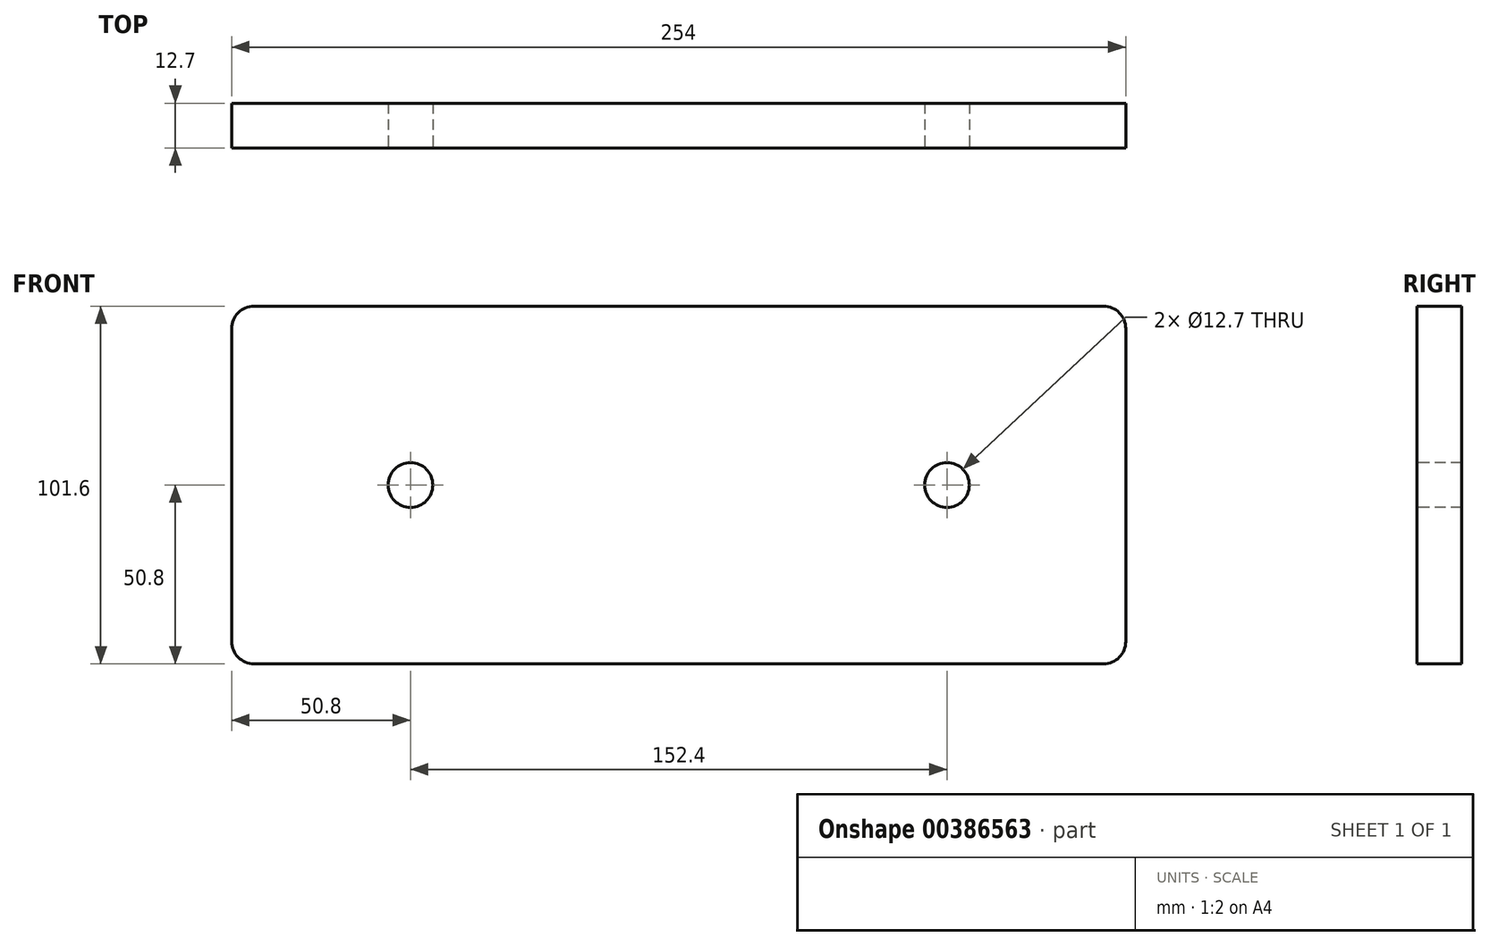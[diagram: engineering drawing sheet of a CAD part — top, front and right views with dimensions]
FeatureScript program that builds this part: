
annotation { "Feature Type Name" : "Feature", "Feature Type Description" : "" }
export const myFeature = defineFeature(function(context is Context, id is Id, definition is map)
    precondition{}
    {
        {
            var Q0;
            Q0=qCreatedBy(makeId("Front.planeOp"),FACE);
            var sketch = newSketch(context, id + "F0", { "sketchPlane" : qUnion([Q0])});
            skLineSegment(sketch, "E0.bottom", {"start": v(0, 0) * mm, "end": v(254, 0) * mm});
            skLineSegment(sketch, "E0.top", {"start": v(0, 101.6) * mm, "end": v(254, 101.6) * mm});
            skLineSegment(sketch, "E0.left", {"start": v(0, 0) * mm, "end": v(0, 101.6) * mm});
            skLineSegment(sketch, "E0.right", {"start": v(254, 0) * mm, "end": v(254, 101.6) * mm});
            skSolve(sketch);
        }
        {
            var Q0;
            Q0 = qSketchRegion(id + "F0", true);
            extrude(context, id + "F1", {"entities" : qUnion([Q0]), "depth" : 12.7 * mm});
        }
        {
            var Q0;
            Q0=makeQuery(id+"F1.opExtrude","CAP_FACE",FACE,{"disambiguationData":[OSD([sQuery(id+"F0.wireOp",EDGE,"E0.bottom"),sQuery(id+"F0.wireOp",EDGE,"E0.top"),sQuery(id+"F0.wireOp",EDGE,"E0.left"),sQuery(id+"F0.wireOp",EDGE,"E0.right")])],"isStart":false});
            var sketch = newSketch(context, id + "F2", { "sketchPlane" : qUnion([Q0])});
            skPoint(sketch, "E1", {"position": v(50.8, 50.8) * mm});
            skPoint(sketch, "E2", {"position": v(203.2, 50.8) * mm});
            skSolve(sketch);
        }
        {
            var Q0;
            Q0=sQuery(id+"F2.wireOp",VERTEX,"E1");
            var Q1;
            Q1=sQuery(id+"F2.wireOp",VERTEX,"E2");
            var Q2;
            Q2=makeQuery(id+"F1.opExtrude","SWEPT_BODY",BODY,{"disambiguationData":[OSD([sQuery(id+"F0.wireOp",EDGE,"E0.bottom"),sQuery(id+"F0.wireOp",EDGE,"E0.top"),sQuery(id+"F0.wireOp",EDGE,"E0.left"),sQuery(id+"F0.wireOp",EDGE,"E0.right")])]});
            hole(context, id + "F3", {"style" : HoleStyle.SIMPLE, "endStyle" : HoleEndStyle.THROUGH, "holeDiameter" : 12.7 * mm, "isTappedThrough" : true, "tappedDepth" : 12.7 * mm, "tapClearance" : 3, "locations" : qUnion([Q0, Q1]), "scope" : qUnion([Q2])});
        }
        {
            var Q0;
            Q0=makeQuery(id+"F1.opExtrude","SWEPT_EDGE",EDGE,{"disambiguationData":[OSD([sQuery(id+"F0.wireOp",EDGE,"E0.top"),sQuery(id+"F0.wireOp",EDGE,"E0.left")])]});
            var Q1;
            Q1=makeQuery(id+"F1.opExtrude","SWEPT_EDGE",EDGE,{"disambiguationData":[OSD([sQuery(id+"F0.wireOp",EDGE,"E0.bottom"),sQuery(id+"F0.wireOp",EDGE,"E0.left")])]});
            var Q2;
            Q2=makeQuery(id+"F1.opExtrude","SWEPT_EDGE",EDGE,{"disambiguationData":[OSD([sQuery(id+"F0.wireOp",EDGE,"E0.top"),sQuery(id+"F0.wireOp",EDGE,"E0.right")])]});
            var Q3;
            Q3=makeQuery(id+"F1.opExtrude","SWEPT_EDGE",EDGE,{"disambiguationData":[OSD([sQuery(id+"F0.wireOp",EDGE,"E0.bottom"),sQuery(id+"F0.wireOp",EDGE,"E0.right")])]});
            fillet(context, id + "F4", {"entities" : qUnion([Q0, Q1, Q2, Q3]), "radius" : 6.35 * mm, "tangentPropagation" : true, "allowEdgeOverflow" : false});
        }
    });
